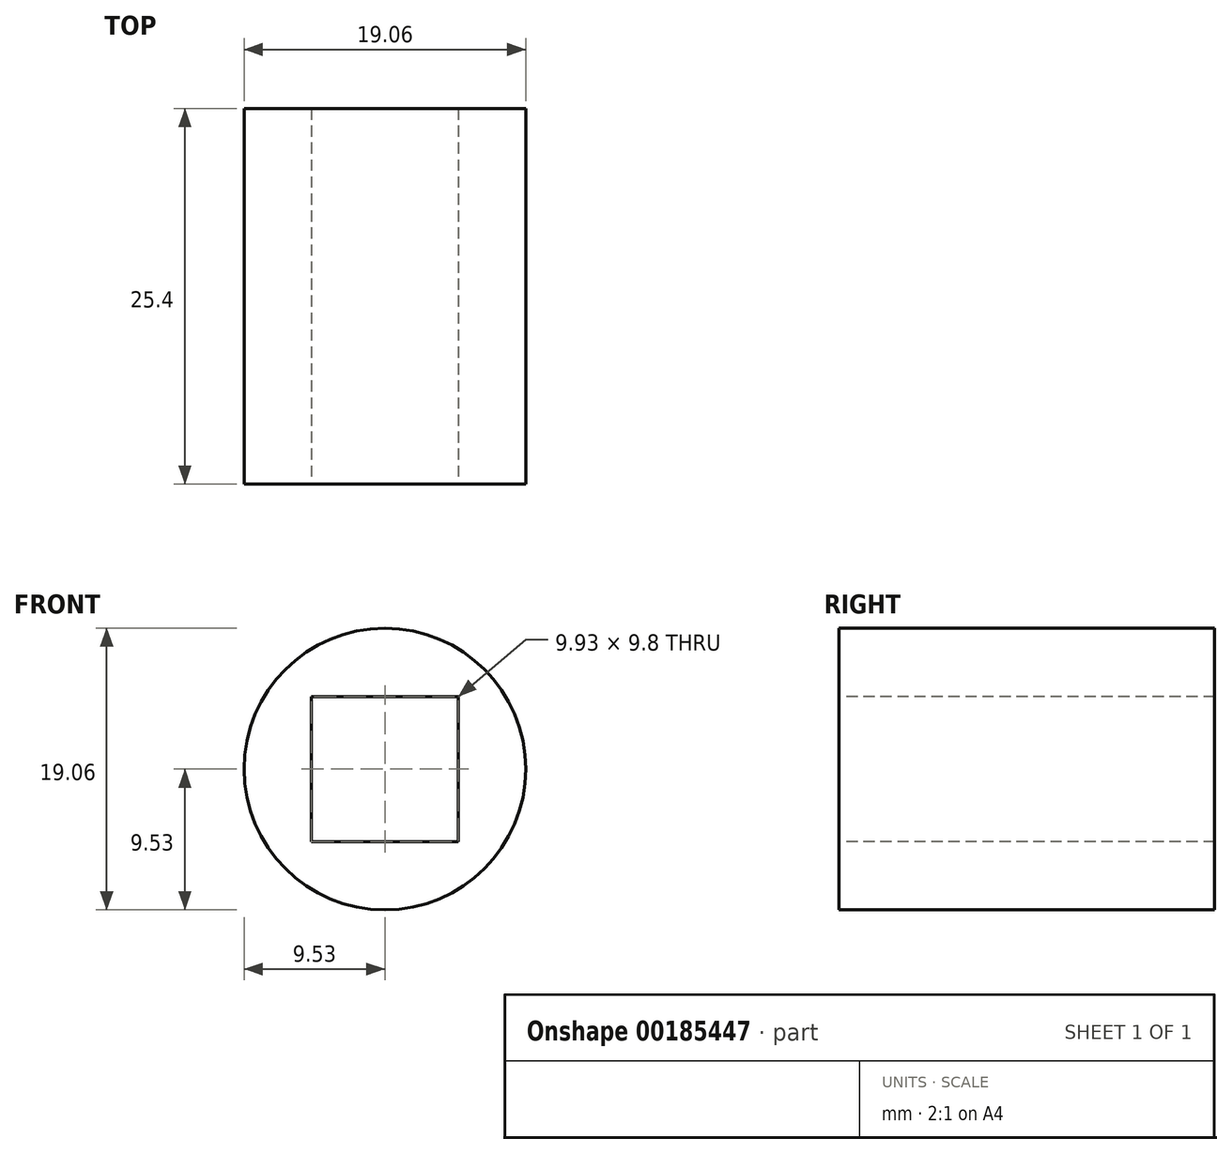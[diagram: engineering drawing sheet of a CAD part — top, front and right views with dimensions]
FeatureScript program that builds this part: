
annotation { "Feature Type Name" : "Feature", "Feature Type Description" : "" }
export const myFeature = defineFeature(function(context is Context, id is Id, definition is map)
    precondition{}
    {
        {
            var Q0;
            Q0=qCreatedBy(makeId("Front.planeOp"),FACE);
            var sketch = newSketch(context, id + "F0", { "sketchPlane" : qUnion([Q0])});
            skCircle(sketch, "E0", {"center": v(0, 0) * mm, "radius": 9.53 * mm});
            skSolve(sketch);
        }
        {
            var Q0;
            Q0=makeQuery(id+"F0.imprint","IMPRINT",FACE,{"disambiguationData":[TD([[makeQuery(id+"F0.imprint","IMPRINT",EDGE,{"derivedFrom":sQuery(id+"F0.wireOp",EDGE,"E0")}),1.0]])]});
            extrude(context, id + "F1", {"entities" : qUnion([Q0]), "depth" : 25.4 * mm});
        }
        {
            var Q0;
            Q0=makeQuery(id+"F1.opExtrude","CAP_FACE",FACE,{"disambiguationData":[OSD([sQuery(id+"F0.wireOp",EDGE,"E0")])],"isStart":false});
            var sketch = newSketch(context, id + "F2", { "sketchPlane" : qUnion([Q0])});
            skLineSegment(sketch, "E1.bottom", {"start": v(4.97, -4.9) * mm, "end": v(-4.97, -4.9) * mm});
            skLineSegment(sketch, "E1.top", {"start": v(4.97, 4.9) * mm, "end": v(-4.97, 4.9) * mm});
            skLineSegment(sketch, "E1.left", {"start": v(4.97, -4.9) * mm, "end": v(4.97, 4.9) * mm});
            skLineSegment(sketch, "E1.right", {"start": v(-4.97, -4.9) * mm, "end": v(-4.97, 4.9) * mm});
            skPoint(sketch, "E1.middle", {"position": v(0, 0) * mm});
            skSolve(sketch);
        }
        {
            var Q0;
            Q0=makeQuery(id+"F2.imprint","IMPRINT",FACE,{"disambiguationData":[TD([[makeQuery(id+"F2.imprint","IMPRINT",EDGE,{"derivedFrom":sQuery(id+"F2.wireOp",EDGE,"E1.bottom")}),-1.0]])]});
            extrude(context, id + "F3", {"entities" : qUnion([Q0]), "operationType" : NewBodyOperationType.REMOVE, "endBound" : BoundingType.THROUGH_ALL, "oppositeDirection" : true, "depth" : 25.4 * mm});
        }
    });
